# Revit family: Hager-GOLF-Hollow_wall-IP40-With_Cover-With_DIN-Hosted-FR-fr
name_source: partatom
category: Electrical Equipment
units: mm (PartAtom-declared; Revit-internal decimal feet)

## family parameters
Cut with Voids When Loaded = No
Host = Face
Maintain Annotation Orientation = Yes
Panel Configuration = Two Columns, Circuits Across
Part Type = Panelboard
Room Calculation Point = No
Round Connector Dimension = Use Diameter
Shared = No

## types (10) — shared parameters
BC_MODEL_ID = 1554321
BC_OBJECT_ID = 513871
BC_OBJECT_VERSION = #3
Code hager = ADD-EC000214_EU
EF000003 - mode de pose = mur creux
EF000007 - couleur = blanc
EF000024 - résistant aux UV = No
EF000049 - profondeur = 97 mm  [stored 0.318241 ft]
EF000116 - numéro RAL = 9010
EF000118 - avec cadre/support de montage = No
EF000218 - profondeur d'encastrement = 72 mm  [stored 0.23622 ft]
EF001062 - finition CEM = No
EF001088 - possibilité de montage en saillie = Yes
EF001134 - rail DIN = Yes
EF004462 - type de fermeture = autre
EF005474 - indice de protection (IP) = IP40
EF006244 - couvercle/porte transparent(e) = No
EF006306 - avec serrure = No
EF009212 - finition du couvercle = fermé
EF015776 - borne de mise à la terre = Yes
EF015941 - porte pour transmission du signal = Yes
ETIM class code = EC000214
ETIM class name = Small distribution board
HG000001-nombre de colonnes = 1
HG000002-avec porte = Yes
HG000003-Gamme = GOLF
HG000005-Epaisseur = 2 mm  [stored 0.00656168 ft]
HG000006-Encastré = Yes
HG000009-Porte à double battant = No
HG000010-Portes asymétriques = No
HG000011-Rangées du bas vides = No
HG000012-Angle de pivotement de la porte = 90.00°
HG000013-Porte à gauche = No
HG000014-Porte à droite = Yes
HG000015-Visibilité de l'emprise de la porte = Yes
HG000016-Visibilité de la porte 3D = Yes
HG000017-Distance entre pôles = 18 mm  [stored 0.0590551 ft]
HG000060-RAL-number = 9010
HG000099-ID modèle Onfly = 507532
Manufacturer = Hager
Name = GOLF-Hollow_wall-IP40-With_Cover-With_DIN-FR
Name BIM&CO = Electricity
Name hager = ADD_Enclosures_EC000214
Uniformat = Low Tension Service & Dist.
Uniformat code = D501001
zero-valued in all types: Default Elevation, EF001131 - profondeur intérieure, HG000007-Nombre de colonnes vides, HG000008-Nombre de rangées vides

## per-type parameters (varying)
| type | BC_VARIANT_ID | EF000008 - largeur | EF000040 - hauteur | EF000266 - nombre de rangées | EF000332 - hauteur d'encastrement | EF000846 - largeur d'encastrement | EF002950 - largeur en nombre de modules | EF015777 - borne à conducteur neutre | HG000004-Référence fabricant | HGEF000266-Nombre de rangées | HGEF0002950-largeur en nombre de modules |
| GOLF-Hollow_wall_W204_H225_D97_4_Modular_Spacing-VF104PR | 1178920 | 204 mm | 225 mm  [stored 0.738189 ft] | 1 | 189 mm  [stored 0.620079 ft] | 170 mm  [stored 0.557743 ft] | 4 | No | VF104PR | 1 | 4 |
| GOLF-Hollow_wall_W275_H225_D97_8_Modular_Spacing-VF108PR | 1178921 | 275 mm | 225 mm  [stored 0.738189 ft] | 1 | 189 mm  [stored 0.620079 ft] | 242 mm  [stored 0.793963 ft] | 8 | No | VF108PR | 1 | 8 |
| GOLF-Hollow_wall_W352_H293_D97_12_Modular_Spacing-VF112PR | 1178922 | 352 mm  [stored 1.15486 ft] | 293 mm | 1 | 257 mm  [stored 0.843176 ft] | 318 mm  [stored 1.04331 ft] | 12 | No | VF112PR | 1 | 12 |
| GOLF-Hollow_wall_W460_H293_D97_18_Modular_Spacing-VF118PR | 1178923 | 460 mm  [stored 1.50919 ft] | 293 mm | 1 | 257 mm  [stored 0.843176 ft] | 426 mm  [stored 1.39764 ft] | 18 | No | VF118PR | 1 | 18 |
| GOLF-Hollow_wall_W382_H418_D97_12_Modular_Spacing-VF212PR | 1178924 | 382 mm  [stored 1.25328 ft] | 418 mm  [stored 1.37139 ft] | 2 | 382 mm  [stored 1.25328 ft] | 318 mm  [stored 1.04331 ft] | 12 | Yes | VF212PR | 2 | 12 |
| GOLF-Hollow_wall_W460_H418_D97_18_Modular_Spacing-VF218PR | 1178925 | 460 mm  [stored 1.50919 ft] | 418 mm  [stored 1.37139 ft] | 2 | 382 mm  [stored 1.25328 ft] | 426 mm  [stored 1.39764 ft] | 18 | Yes | VF218PR | 2 | 18 |
| GOLF-Hollow_wall_W352_H543_D97_12_Modular_Spacing-VF312PR | 1178926 | 352 mm  [stored 1.15486 ft] | 543 mm  [stored 1.7815 ft] | 3 | 507 mm  [stored 1.66339 ft] | 318 mm  [stored 1.04331 ft] | 12 | Yes | VF312PR | 3 | 12 |
| GOLF-Hollow_wall_W460_H543_D97_18_Modular_Spacing-VF318PR | 1178927 | 460 mm  [stored 1.50919 ft] | 543 mm  [stored 1.7815 ft] | 3 | 507 mm  [stored 1.66339 ft] | 426 mm  [stored 1.39764 ft] | 18 | Yes | VF318PR | 3 | 18 |
| GOLF-Hollow_wall_W352_H688_D97_12_Modular_Spacing-VF412PR | 1178928 | 352 mm  [stored 1.15486 ft] | 688 mm  [stored 2.25722 ft] | 4 | 652 mm  [stored 2.13911 ft] | 318 mm  [stored 1.04331 ft] | 12 | Yes | VF412PR | 4 | 12 |
| GOLF-Hollow_wall_W460_H688_D97_18_Modular_Spacing-VF418PR | 1178929 | 460 mm  [stored 1.50919 ft] | 688 mm  [stored 2.25722 ft] | 4 | 652 mm  [stored 2.13911 ft] | 426 mm  [stored 1.39764 ft] | 18 | Yes | VF418PR | 4 | 18 |

note: column(s) folded — value = type name in every type: Reference

note: [stored X ft] marks values corroborated as IEEE doubles in the binary element streams (Revit-internal decimal feet)

## geometry (parser evidence)
native form markers: Sweep x14
no freeform markers — native parametric forms only
